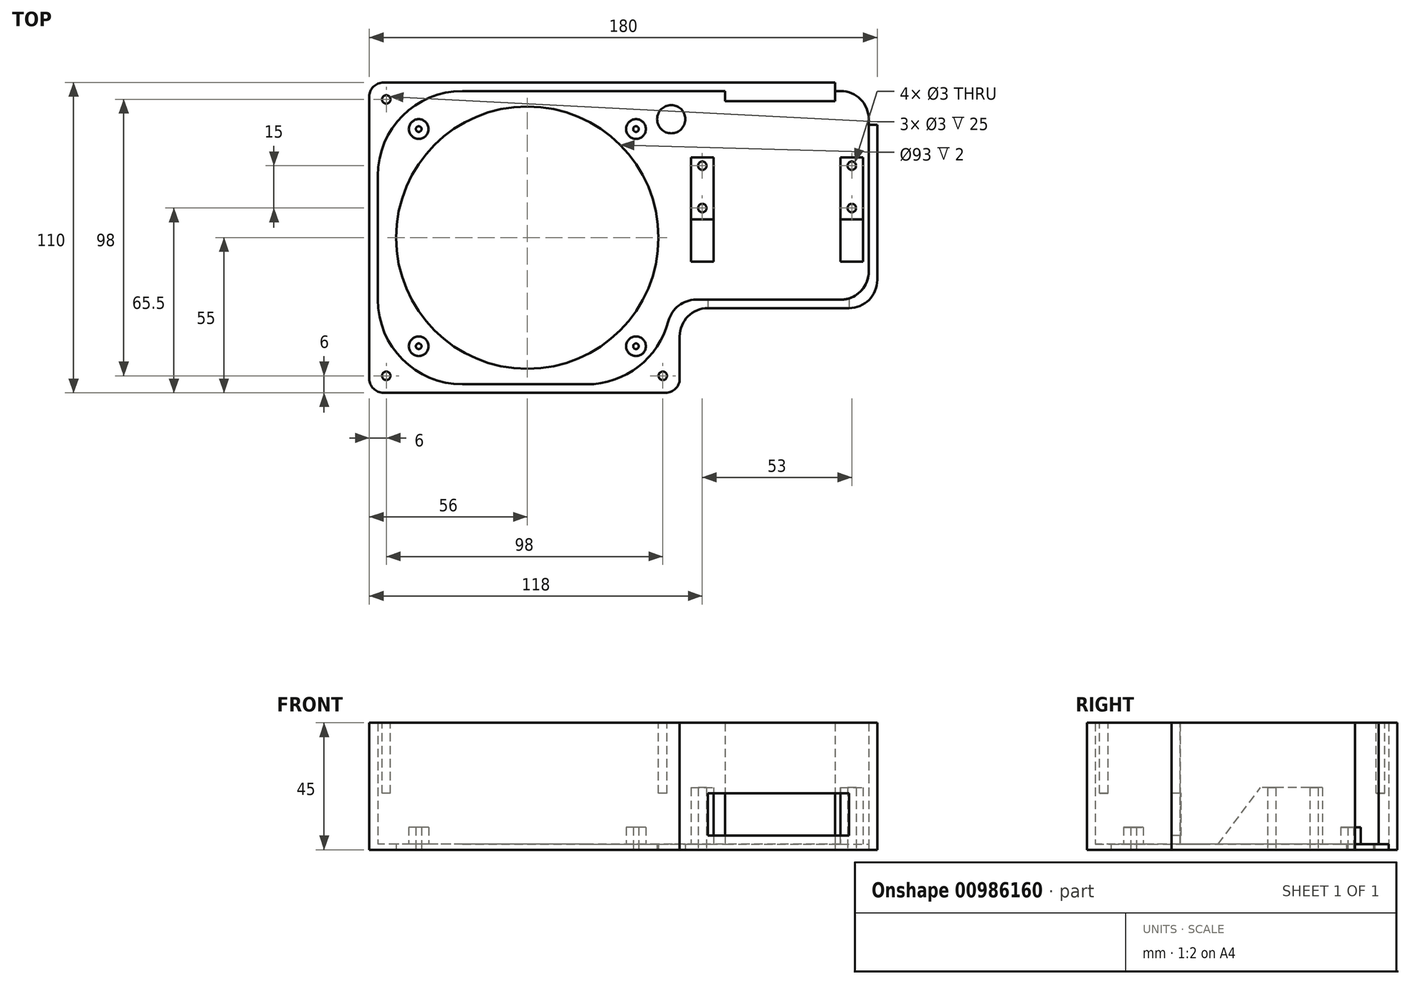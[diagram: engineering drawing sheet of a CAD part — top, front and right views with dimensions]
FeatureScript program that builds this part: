
annotation { "Feature Type Name" : "Feature", "Feature Type Description" : "" }
export const myFeature = defineFeature(function(context is Context, id is Id, definition is map)
    precondition{}
    {
        {
            var Q0;
            Q0=qCreatedBy(makeId("Top.planeOp"),FACE);
            var sketch = newSketch(context, id + "F0", { "sketchPlane" : qUnion([Q0])});
            skLineSegment(sketch, "E0.top", {"start": v(0, 110) * mm, "end": v(180, 110) * mm});
            skLineSegment(sketch, "E0.left", {"start": v(0, 0) * mm, "end": v(0, 110) * mm});
            skLineSegment(sketch, "E1.bottom", {"start": v(167, 83.5) * mm, "end": v(175, 83.5) * mm});
            skLineSegment(sketch, "E1.top", {"start": v(167, 46.5) * mm, "end": v(175, 46.5) * mm});
            skLineSegment(sketch, "E1.left", {"start": v(167, 83.5) * mm, "end": v(167, 46.5) * mm});
            skLineSegment(sketch, "E1.right", {"start": v(175, 83.5) * mm, "end": v(175, 46.5) * mm});
            skLineSegment(sketch, "E2.bottom", {"start": v(114, 83.5) * mm, "end": v(122, 83.5) * mm});
            skLineSegment(sketch, "E2.top", {"start": v(114, 46.5) * mm, "end": v(122, 46.5) * mm});
            skLineSegment(sketch, "E2.left", {"start": v(114, 83.5) * mm, "end": v(114, 46.5) * mm});
            skLineSegment(sketch, "E2.right", {"start": v(122, 83.5) * mm, "end": v(122, 46.5) * mm});
            skCircle(sketch, "E3", {"center": v(118, 80.5) * mm, "radius": 1.5 * mm});
            skCircle(sketch, "E4", {"center": v(118, 65.5) * mm, "radius": 1.5 * mm});
            skCircle(sketch, "E5", {"center": v(171, 80.5) * mm, "radius": 1.5 * mm});
            skCircle(sketch, "E6", {"center": v(171, 65.5) * mm, "radius": 1.5 * mm});
            skCircle(sketch, "E7", {"center": v(56, 55) * mm, "radius": 46.5 * mm});
            skLineSegment(sketch, "E8", {"start": v(180, 110) * mm, "end": v(180, 30) * mm});
            skLineSegment(sketch, "E9", {"start": v(180, 30) * mm, "end": v(110, 30) * mm});
            skLineSegment(sketch, "E10", {"start": v(110, 30) * mm, "end": v(110, 0) * mm});
            skLineSegment(sketch, "E11", {"start": v(110, 0) * mm, "end": v(0, 0) * mm});
            skLineSegment(sketch, "E12.top", {"start": v(110, 3) * mm, "end": v(0, 3) * mm});
            skLineSegment(sketch, "E12.left", {"start": v(110, 0) * mm, "end": v(110, 3) * mm});
            skLineSegment(sketch, "E12.right", {"start": v(0, 0) * mm, "end": v(0, 3) * mm});
            skLineSegment(sketch, "E13.bottom", {"start": v(0, 110) * mm, "end": v(3, 110) * mm});
            skLineSegment(sketch, "E13.top", {"start": v(0, 3) * mm, "end": v(3, 3) * mm});
            skLineSegment(sketch, "E13.left", {"start": v(0, 110) * mm, "end": v(0, 3) * mm});
            skLineSegment(sketch, "E13.right", {"start": v(3, 110) * mm, "end": v(3, 3) * mm});
            skLineSegment(sketch, "E14.bottom", {"start": v(3, 107) * mm, "end": v(180, 107) * mm});
            skLineSegment(sketch, "E14.top", {"start": v(3, 110) * mm, "end": v(180, 110) * mm});
            skLineSegment(sketch, "E14.left", {"start": v(3, 107) * mm, "end": v(3, 110) * mm});
            skLineSegment(sketch, "E14.right", {"start": v(180, 107) * mm, "end": v(180, 110) * mm});
            skLineSegment(sketch, "E15.bottom", {"start": v(180, 107) * mm, "end": v(177, 107) * mm});
            skLineSegment(sketch, "E15.top", {"start": v(180, 30) * mm, "end": v(177, 30) * mm});
            skLineSegment(sketch, "E15.left", {"start": v(180, 107) * mm, "end": v(180, 30) * mm});
            skLineSegment(sketch, "E15.right", {"start": v(177, 107) * mm, "end": v(177, 30) * mm});
            skLineSegment(sketch, "E16.bottom", {"start": v(110, 30) * mm, "end": v(107, 30) * mm});
            skLineSegment(sketch, "E16.top", {"start": v(110, 3) * mm, "end": v(107, 3) * mm});
            skLineSegment(sketch, "E16.left", {"start": v(110, 30) * mm, "end": v(110, 3) * mm});
            skLineSegment(sketch, "E16.right", {"start": v(107, 30) * mm, "end": v(107, 3) * mm});
            skLineSegment(sketch, "E17.bottom", {"start": v(177, 30) * mm, "end": v(107, 30) * mm});
            skLineSegment(sketch, "E17.top", {"start": v(177, 33) * mm, "end": v(107, 33) * mm});
            skLineSegment(sketch, "E17.left", {"start": v(177, 30) * mm, "end": v(177, 33) * mm});
            skLineSegment(sketch, "E17.right", {"start": v(107, 30) * mm, "end": v(107, 33) * mm});
            skLineSegment(sketch, "E18.bottom", {"start": v(177, 107) * mm, "end": v(180, 107) * mm});
            skLineSegment(sketch, "E18.top", {"start": v(177, 95) * mm, "end": v(180, 95) * mm});
            skLineSegment(sketch, "E18.left", {"start": v(177, 107) * mm, "end": v(177, 95) * mm});
            skLineSegment(sketch, "E18.right", {"start": v(180, 107) * mm, "end": v(180, 95) * mm});
            skLineSegment(sketch, "E19.bottom", {"start": v(180, 110) * mm, "end": v(165, 110) * mm});
            skLineSegment(sketch, "E19.top", {"start": v(180, 107) * mm, "end": v(165, 107) * mm});
            skLineSegment(sketch, "E19.left", {"start": v(180, 110) * mm, "end": v(180, 107) * mm});
            skLineSegment(sketch, "E19.right", {"start": v(165, 110) * mm, "end": v(165, 107) * mm});
            skCircle(sketch, "E20", {"center": v(17.5, 93.5) * mm, "radius": 3.5 * mm});
            skCircle(sketch, "E21", {"center": v(94.5, 93.5) * mm, "radius": 3.5 * mm});
            skCircle(sketch, "E22", {"center": v(94.5, 16.5) * mm, "radius": 3.5 * mm});
            skCircle(sketch, "E23", {"center": v(17.5, 16.5) * mm, "radius": 3.5 * mm});
            skLineSegment(sketch, "E24", {"start": v(56, 55) * mm, "end": v(106.17, 55) * mm, "construction": true});
            skLineSegment(sketch, "E25", {"start": v(56, 55) * mm, "end": v(4.12, 55) * mm, "construction": true});
            skLineSegment(sketch, "E26", {"start": v(56, 55) * mm, "end": v(56, 105.52) * mm, "construction": true});
            skLineSegment(sketch, "E27", {"start": v(56, 55) * mm, "end": v(56, 5.78) * mm, "construction": true});
            skCircle(sketch, "E28", {"center": v(94.5, 93.5) * mm, "radius": 1 * mm});
            skCircle(sketch, "E29", {"center": v(17.5, 93.5) * mm, "radius": 1 * mm});
            skCircle(sketch, "E30", {"center": v(17.5, 16.5) * mm, "radius": 1 * mm});
            skCircle(sketch, "E31", {"center": v(94.5, 16.5) * mm, "radius": 1 * mm});
            skCircle(sketch, "E32", {"center": v(107, 97) * mm, "radius": 5 * mm});
            skLineSegment(sketch, "E33.bottom", {"start": v(126.13, 107) * mm, "end": v(165, 107) * mm});
            skLineSegment(sketch, "E33.top", {"start": v(126.13, 103.38) * mm, "end": v(165, 103.38) * mm});
            skLineSegment(sketch, "E33.left", {"start": v(126.13, 107) * mm, "end": v(126.13, 103.38) * mm});
            skLineSegment(sketch, "E33.right", {"start": v(165, 107) * mm, "end": v(165, 103.38) * mm});
            skSolve(sketch);
        }
        {
            var Q0;
            Q0=makeQuery(id+"F0.imprint","IMPRINT",FACE,{"disambiguationData":[TD([[makeQuery(id+"F0.imprint","IMPRINT",EDGE,{"derivedFrom":sQuery(id+"F0.wireOp",EDGE,"E1.bottom")}),1.0]])]});
            extrude(context, id + "F1", {"entities" : qUnion([Q0]), "depth" : 2 * mm, "offsetDistance" : 25 * mm});
        }
        {
            var Q0;
            Q0=makeQuery(id+"F0.imprint","IMPRINT",FACE,{"disambiguationData":[TD([[makeQuery(id+"F0.imprint","IMPRINT",EDGE,{"derivedFrom":sQuery(id+"F0.wireOp",EDGE,"E2.bottom")}),-1.0]])]});
            var Q1;
            Q1=makeQuery(id+"F0.imprint","IMPRINT",FACE,{"disambiguationData":[TD([[makeQuery(id+"F0.imprint","IMPRINT",EDGE,{"derivedFrom":sQuery(id+"F0.wireOp",EDGE,"E1.bottom")}),-1.0]])]});
            extrude(context, id + "F2", {"entities" : qUnion([Q0, Q1]), "operationType" : NewBodyOperationType.ADD, "depth" : 22 * mm, "offsetDistance" : 25 * mm});
        }
        {
            var Q0;
            {var subQ0=sQuery(id+"F0.wireOp",EDGE,"E19.right");Q0=makeQuery(id+"F0.imprint","IMPRINT",FACE,{"disambiguationData":[TD([[makeQuery(id+"F0.imprint","IMPRINT",EDGE,{"derivedFrom":subQ0}),-1.0]])]});}
            var Q1;
            {var subQ0=sQuery(id+"F0.wireOp",EDGE,"E13.right");var subQ6=sQuery(id+"F0.wireOp",EDGE,"E0.top");var subQ8=makeQuery(id+"F0.imprint","INTERSECT",VERTEX,{"derivedFrom":[subQ6,subQ0]});Q1=makeQuery(id+"F0.imprint","IMPRINT",FACE,{"disambiguationData":[TD([[makeQuery(id+"F0.imprint","IMPRINT",EDGE,{"disambiguationData":[TD([[subQ8,1.0]])],"derivedFrom":subQ6}),-1.0]])]});}
            var Q2;
            {var subQ5=sQuery(id+"F0.wireOp",EDGE,"E11");Q2=makeQuery(id+"F0.imprint","IMPRINT",FACE,{"disambiguationData":[TD([[makeQuery(id+"F0.imprint","IMPRINT",EDGE,{"derivedFrom":subQ5}),-1.0]])]});}
            var Q3;
            Q3=makeQuery(id+"F0.imprint","IMPRINT",FACE,{"disambiguationData":[TD([[makeQuery(id+"F0.imprint","IMPRINT",EDGE,{"derivedFrom":sQuery(id+"F0.wireOp",EDGE,"E15.bottom")}),1.0]])]});
            var Q4;
            Q4=makeQuery(id+"F0.imprint","IMPRINT",FACE,{"disambiguationData":[TD([[makeQuery(id+"F0.imprint","IMPRINT",EDGE,{"derivedFrom":sQuery(id+"F0.wireOp",EDGE,"E16.bottom")}),1.0]])]});
            var Q5;
            {var subQ0=sQuery(id+"F0.wireOp",EDGE,"E16.bottom");Q5=makeQuery(id+"F0.imprint","IMPRINT",FACE,{"disambiguationData":[TD([[makeQuery(id+"F0.imprint","IMPRINT",EDGE,{"derivedFrom":subQ0}),1.0]])]});}
            var Q6;
            {var subQ1=sQuery(id+"F0.wireOp",EDGE,"E16.bottom");Q6=makeQuery(id+"F0.imprint","IMPRINT",FACE,{"disambiguationData":[TD([[makeQuery(id+"F0.imprint","IMPRINT",EDGE,{"derivedFrom":subQ1}),-1.0]])]});}
            var Q7;
            {var subQ0=sQuery(id+"F0.wireOp",EDGE,"E18.top");Q7=makeQuery(id+"F0.imprint","IMPRINT",FACE,{"disambiguationData":[TD([[makeQuery(id+"F0.imprint","IMPRINT",EDGE,{"derivedFrom":subQ0}),-1.0]])]});}
            var Q8;
            Q8=makeQuery(id+"F0.imprint","IMPRINT",FACE,{"disambiguationData":[TD([[makeQuery(id+"F0.imprint","IMPRINT",EDGE,{"derivedFrom":sQuery(id+"F0.wireOp",EDGE,"E33.top")}),1.0]])]});
            extrude(context, id + "F3", {"entities" : qUnion([Q0, Q1, Q2, Q3, Q4, Q5, Q6, Q7, Q8]), "operationType" : NewBodyOperationType.ADD, "depth" : 45 * mm, "offsetDistance" : 25 * mm});
        }
        {
            var Q0;
            Q0=makeQuery(id+"F3.opExtrude","SWEPT_EDGE",EDGE,{"disambiguationData":[OSD([sQuery(id+"F0.wireOp",EDGE,"E13.right"),sQuery(id+"F0.wireOp",EDGE,"E14.bottom")])]});
            var Q1;
            Q1=makeQuery(id+"F3.opExtrude","SWEPT_EDGE",EDGE,{"disambiguationData":[OSD([sQuery(id+"F0.wireOp",EDGE,"E12.top"),sQuery(id+"F0.wireOp",EDGE,"E13.right")])]});
            var Q2;
            Q2=makeQuery(id+"F3.opExtrude","SWEPT_EDGE",EDGE,{"disambiguationData":[OSD([sQuery(id+"F0.wireOp",EDGE,"E12.top"),sQuery(id+"F0.wireOp",EDGE,"E16.right")])]});
            fillet(context, id + "F4", {"entities" : qUnion([Q0, Q1, Q2]), "radius" : 30 * mm, "tangentPropagation" : true, "allowEdgeOverflow" : false});
        }
        {
            var Q0;
            Q0=makeQuery(id+"F3.opExtrude","SWEPT_EDGE",EDGE,{"disambiguationData":[OSD([sQuery(id+"F0.wireOp",EDGE,"E15.right"),sQuery(id+"F0.wireOp",EDGE,"E17.top")])]});
            var Q1;
            Q1=makeQuery(id+"F3.opExtrude","SWEPT_EDGE",EDGE,{"disambiguationData":[OSD([sQuery(id+"F0.wireOp",EDGE,"E8"),sQuery(id+"F0.wireOp",EDGE,"E9")])]});
            var Q2;
            Q2=makeQuery(id+"F3.opExtrude","SWEPT_EDGE",EDGE,{"disambiguationData":[OSD([sQuery(id+"F0.wireOp",EDGE,"E9"),sQuery(id+"F0.wireOp",EDGE,"E10"),sQuery(id+"F0.wireOp",EDGE,"E16.bottom")])]});
            var Q3;
            Q3=makeQuery(id+"F3.opExtrude","SWEPT_EDGE",EDGE,{"disambiguationData":[OSD([sQuery(id+"F0.wireOp",EDGE,"E17.top"),sQuery(id+"F0.wireOp",EDGE,"E17.right")])]});
            var Q4;
            Q4=makeQuery(id+"F1.opExtrude","SWEPT_EDGE",EDGE,{"disambiguationData":[OSD([sQuery(id+"F0.wireOp",EDGE,"E14.bottom"),sQuery(id+"F0.wireOp",EDGE,"E15.right")])]});
            var Q5;
            Q5=makeQuery(id+"F4.opFillet","BLEND_EDGE",EDGE,{"blendedFrom":[makeQuery(id+"F3.opExtrude","SWEPT_EDGE",EDGE,{"disambiguationData":[OSD([sQuery(id+"F0.wireOp",EDGE,"E12.top"),sQuery(id+"F0.wireOp",EDGE,"E16.right")])]}),makeQuery(id+"F3.opExtrude","SWEPT_FACE",FACE,{"disambiguationData":[OSD([sQuery(id+"F0.wireOp",EDGE,"E17.top")])]})],"blendedInto":[makeQuery(id+"F3.opExtrude","SWEPT_FACE",FACE,{"disambiguationData":[OSD([sQuery(id+"F0.wireOp",EDGE,"E17.top")])]})]});
            fillet(context, id + "F5", {"entities" : qUnion([Q0, Q1, Q2, Q3, Q4, Q5]), "radius" : 10 * mm, "tangentPropagation" : true, "allowEdgeOverflow" : false});
        }
        {
            var Q0;
            Q0=makeQuery(id+"F3.opExtrude","SWEPT_FACE",FACE,{"disambiguationData":[OSD([sQuery(id+"F0.wireOp",EDGE,"E9")])]});
            var sketch = newSketch(context, id + "F6", { "sketchPlane" : qUnion([Q0])});
            skLineSegment(sketch, "E34.bottom", {"start": v(120, 20) * mm, "end": v(170, 20) * mm});
            skLineSegment(sketch, "E34.top", {"start": v(120, 5) * mm, "end": v(170, 5) * mm});
            skLineSegment(sketch, "E34.left", {"start": v(120, 20) * mm, "end": v(120, 5) * mm});
            skLineSegment(sketch, "E34.right", {"start": v(170, 20) * mm, "end": v(170, 5) * mm});
            skSolve(sketch);
        }
        {
            var Q0;
            Q0=makeQuery(id+"F6.imprint","IMPRINT",FACE,{"disambiguationData":[TD([[makeQuery(id+"F6.imprint","IMPRINT",EDGE,{"derivedFrom":sQuery(id+"F6.wireOp",EDGE,"E34.bottom")}),-1.0]])]});
            extrude(context, id + "F7", {"entities" : qUnion([Q0]), "operationType" : NewBodyOperationType.REMOVE, "oppositeDirection" : true, "depth" : 5 * mm, "offsetDistance" : 25 * mm});
        }
        {
            var Q0;
            Q0=makeQuery(id+"F3.opExtrude","SWEPT_EDGE",EDGE,{"disambiguationData":[OSD([sQuery(id+"F0.wireOp",EDGE,"E10"),sQuery(id+"F0.wireOp",EDGE,"E11")])]});
            var Q1;
            Q1=makeQuery(id+"F3.opExtrude","SWEPT_EDGE",EDGE,{"disambiguationData":[OSD([sQuery(id+"F0.wireOp",EDGE,"E0.left"),sQuery(id+"F0.wireOp",EDGE,"E11")])]});
            var Q2;
            Q2=makeQuery(id+"F3.opExtrude","SWEPT_EDGE",EDGE,{"disambiguationData":[OSD([sQuery(id+"F0.wireOp",EDGE,"E0.top"),sQuery(id+"F0.wireOp",EDGE,"E0.left")])]});
            fillet(context, id + "F8", {"entities" : qUnion([Q0, Q1, Q2]), "radius" : 5 * mm, "tangentPropagation" : true, "allowEdgeOverflow" : false});
        }
        {
            var Q0;
            Q0=makeQuery(id+"F0.imprint","IMPRINT",FACE,{"disambiguationData":[TD([[makeQuery(id+"F0.imprint","IMPRINT",EDGE,{"derivedFrom":sQuery(id+"F0.wireOp",EDGE,"E21")}),1.0]])]});
            var Q1;
            Q1=makeQuery(id+"F0.imprint","IMPRINT",FACE,{"disambiguationData":[TD([[makeQuery(id+"F0.imprint","IMPRINT",EDGE,{"derivedFrom":sQuery(id+"F0.wireOp",EDGE,"E20")}),1.0]])]});
            var Q2;
            Q2=makeQuery(id+"F0.imprint","IMPRINT",FACE,{"disambiguationData":[TD([[makeQuery(id+"F0.imprint","IMPRINT",EDGE,{"derivedFrom":sQuery(id+"F0.wireOp",EDGE,"E23")}),1.0]])]});
            var Q3;
            Q3=makeQuery(id+"F0.imprint","IMPRINT",FACE,{"disambiguationData":[TD([[makeQuery(id+"F0.imprint","IMPRINT",EDGE,{"derivedFrom":sQuery(id+"F0.wireOp",EDGE,"E22")}),1.0]])]});
            extrude(context, id + "F9", {"entities" : qUnion([Q0, Q1, Q2, Q3]), "operationType" : NewBodyOperationType.ADD, "depth" : 8 * mm, "offsetDistance" : 25 * mm});
        }
        {
            var Q0;
            Q0=makeQuery(id+"F3.opExtrude","CAP_FACE",FACE,{"disambiguationData":[OSD([sQuery(id+"F0.wireOp",EDGE,"E0.top"),sQuery(id+"F0.wireOp",EDGE,"E0.left"),sQuery(id+"F0.wireOp",EDGE,"E8"),sQuery(id+"F0.wireOp",EDGE,"E9"),sQuery(id+"F0.wireOp",EDGE,"E10"),sQuery(id+"F0.wireOp",EDGE,"E11"),sQuery(id+"F0.wireOp",EDGE,"E12.top"),sQuery(id+"F0.wireOp",EDGE,"E13.right"),sQuery(id+"F0.wireOp",EDGE,"E14.bottom"),sQuery(id+"F0.wireOp",EDGE,"E15.right"),sQuery(id+"F0.wireOp",EDGE,"E16.right"),sQuery(id+"F0.wireOp",EDGE,"E17.top"),sQuery(id+"F0.wireOp",EDGE,"E17.right"),sQuery(id+"F0.wireOp",EDGE,"E18.top"),sQuery(id+"F0.wireOp",EDGE,"E19.right"),sQuery(id+"F0.wireOp",EDGE,"E33.top"),sQuery(id+"F0.wireOp",EDGE,"E33.left"),sQuery(id+"F0.wireOp",EDGE,"E33.right")])],"isStart":false});
            var sketch = newSketch(context, id + "F10", { "sketchPlane" : qUnion([Q0])});
            skCircle(sketch, "E35", {"center": v(6, 104) * mm, "radius": 1.5 * mm});
            skCircle(sketch, "E36", {"center": v(6, 6) * mm, "radius": 1.5 * mm});
            skCircle(sketch, "E37", {"center": v(104, 6) * mm, "radius": 1.5 * mm});
            skLineSegment(sketch, "E38.bottom", {"start": v(165, 110) * mm, "end": v(180, 110) * mm});
            skLineSegment(sketch, "E38.top", {"start": v(165, 95) * mm, "end": v(180, 95) * mm});
            skLineSegment(sketch, "E38.left", {"start": v(165, 110) * mm, "end": v(165, 95) * mm});
            skLineSegment(sketch, "E38.right", {"start": v(180, 110) * mm, "end": v(180, 95) * mm});
            skSolve(sketch);
        }
        {
            var Q0;
            Q0=makeQuery(id+"F10.imprint","IMPRINT",FACE,{"disambiguationData":[TD([[makeQuery(id+"F10.imprint","IMPRINT",EDGE,{"derivedFrom":sQuery(id+"F10.wireOp",EDGE,"E35")}),1.0]])]});
            var Q1;
            Q1=makeQuery(id+"F10.imprint","IMPRINT",FACE,{"disambiguationData":[TD([[makeQuery(id+"F10.imprint","IMPRINT",EDGE,{"derivedFrom":sQuery(id+"F10.wireOp",EDGE,"E36")}),1.0]])]});
            var Q2;
            Q2=makeQuery(id+"F10.imprint","IMPRINT",FACE,{"disambiguationData":[TD([[makeQuery(id+"F10.imprint","IMPRINT",EDGE,{"derivedFrom":sQuery(id+"F10.wireOp",EDGE,"E37")}),1.0]])]});
            extrude(context, id + "F11", {"entities" : qUnion([Q0, Q1, Q2]), "operationType" : NewBodyOperationType.REMOVE, "oppositeDirection" : true, "depth" : 25 * mm, "offsetDistance" : 25 * mm});
        }
        {
            var Q0;
            Q0=makeQuery(id+"F2.opExtrude","CAP_EDGE",EDGE,{"disambiguationData":[OSD([sQuery(id+"F0.wireOp",EDGE,"E2.top")])],"isStart":false});
            var Q1;
            Q1=makeQuery(id+"F2.opExtrude","CAP_EDGE",EDGE,{"disambiguationData":[OSD([sQuery(id+"F0.wireOp",EDGE,"E1.top")])],"isStart":false});
            chamfer(context, id + "F12", {"entities" : qUnion([Q0, Q1]), "chamferType" : ChamferType.TWO_OFFSETS, "width1" : 15 * mm, "oppositeDirection" : false, "width2" : 20 * mm, "tangentPropagation" : true});
        }
    });
